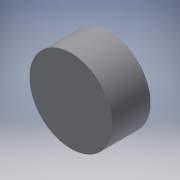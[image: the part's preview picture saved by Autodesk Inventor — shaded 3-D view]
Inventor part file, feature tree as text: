
AUTODESK INVENTOR PART (.ipt)
format: ipt  version: 2016 (Build 200138000, 138)  size: 87,552 bytes
history: native  units: in
note: dims shown in document units (in); Inventor stores cm internally (conversion verified against a paired STEP export)
features: extrude x1, sketch x1
ambient origin geometry x8: Origin, YZ Plane, XZ Plane, XY Plane, X Axis, Y Axis, Z Axis, Center Point
bodies: Solid1 (feature_tree)
feature tree (2):
  extrude  "Extrusion1"  Depth=0.315in TaperAngle=0.0deg
  sketch  "Sketch1"  dims[d0=0.689in d1=0.315in d2=0.0in]
